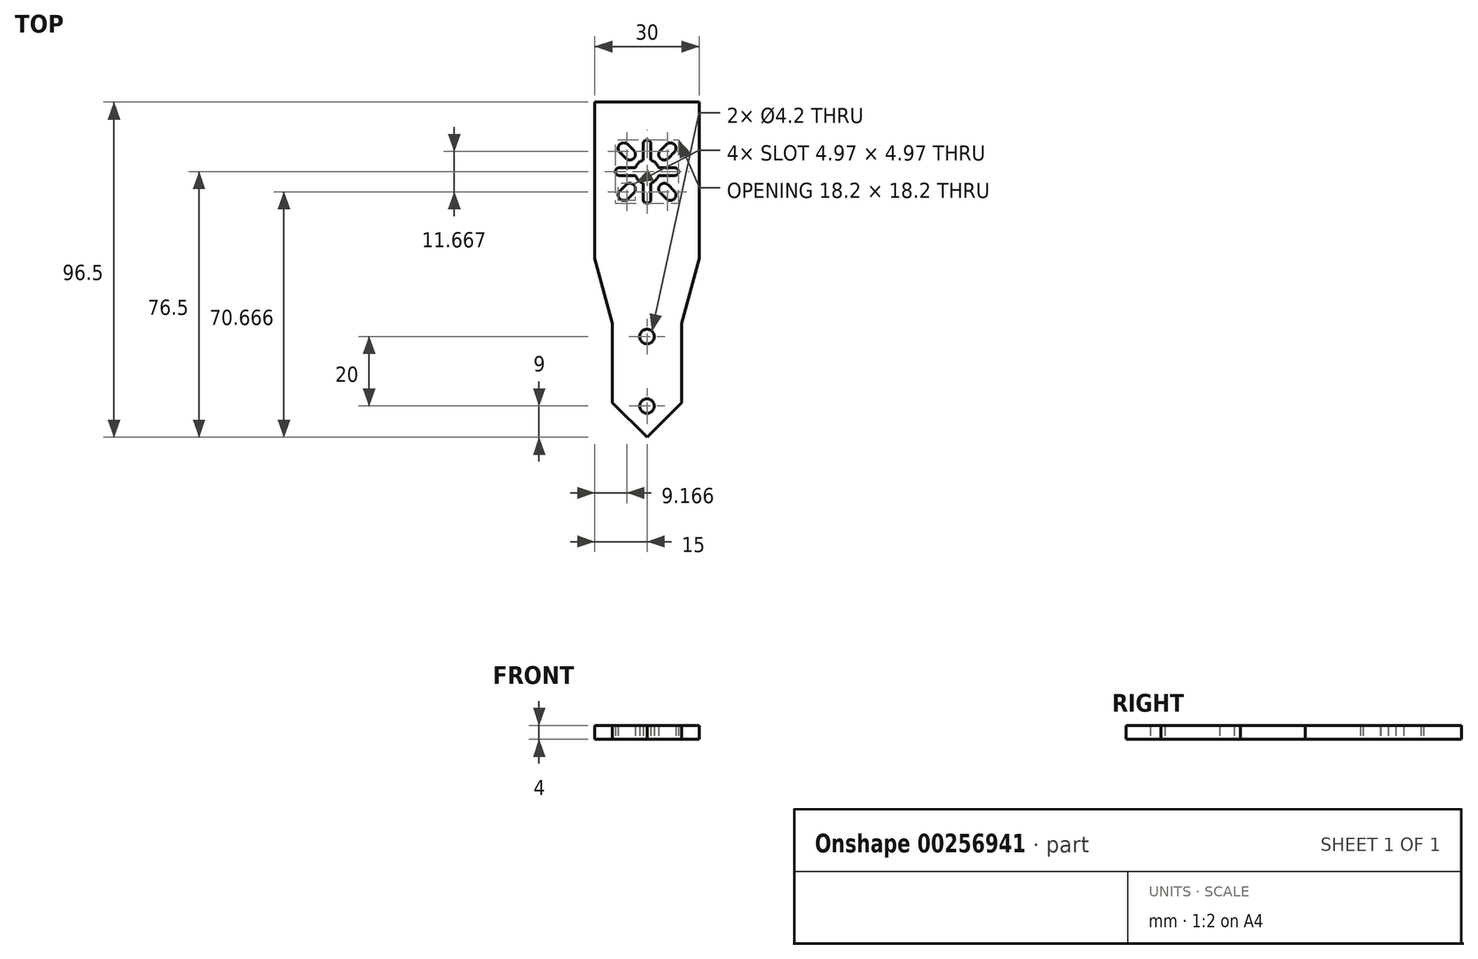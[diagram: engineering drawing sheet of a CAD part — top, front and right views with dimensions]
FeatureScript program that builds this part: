
annotation { "Feature Type Name" : "Feature", "Feature Type Description" : "" }
export const myFeature = defineFeature(function(context is Context, id is Id, definition is map)
    precondition{}
    {
        {
            var Q0;
            Q0=qCreatedBy(makeId("Top.planeOp"),FACE);
            var sketch = newSketch(context, id + "F0", { "sketchPlane" : qUnion([Q0])});
            skLineSegment(sketch, "E0", {"start": v(0, 77.5) * mm, "end": v(0, -77.5) * mm, "construction": true});
            skLineSegment(sketch, "E1", {"start": v(-10, 33.84) * mm, "end": v(-10, 11) * mm});
            skLineSegment(sketch, "E2", {"start": v(-10, 11) * mm, "end": v(0, 1) * mm});
            skLineSegment(sketch, "E3", {"start": v(-10, 33.84) * mm, "end": v(-15, 52.5) * mm});
            skLineSegment(sketch, "E4", {"start": v(-15, 52.5) * mm, "end": v(-15, 97.5) * mm});
            skLineSegment(sketch, "E5", {"start": v(-15, 97.5) * mm, "end": v(15, 97.5) * mm});
            skLineSegment(sketch, "E6.MirrorCS", {"start": v(15, 52.5) * mm, "end": v(15, 97.5) * mm});
            skLineSegment(sketch, "E7.MirrorCS", {"start": v(10, 33.84) * mm, "end": v(15, 52.5) * mm});
            skLineSegment(sketch, "E8.MirrorCS", {"start": v(10, 11) * mm, "end": v(0, 1) * mm});
            skLineSegment(sketch, "E9.MirrorCS", {"start": v(10, 33.84) * mm, "end": v(10, 11) * mm});
            skCircle(sketch, "E10", {"center": v(0, 10) * mm, "radius": 2.1 * mm});
            skCircle(sketch, "E11", {"center": v(0, 30) * mm, "radius": 2.1 * mm});
            skArc(sketch, "E12", {"start": v(-5.59, 85.35) * mm, "mid": v(-7.85, 85.35) * mm, "end": v(-7.85, 83.09) * mm});
            skArc(sketch, "E13", {"start": v(-6.08, 81.32) * mm, "mid": v(-3.82, 81.32) * mm, "end": v(-3.82, 83.58) * mm});
            skLineSegment(sketch, "E14", {"start": v(-5.59, 85.35) * mm, "end": v(-3.82, 83.58) * mm});
            skLineSegment(sketch, "E15", {"start": v(-7.85, 83.09) * mm, "end": v(-6.08, 81.32) * mm});
            skArc(sketch, "E16", {"start": v(-1.1, 80.82) * mm, "mid": v(-2.47, 79.97) * mm, "end": v(-3.32, 78.6) * mm});
            skArc(sketch, "E17", {"start": v(1.1, 85.5) * mm, "mid": v(0, 86.6) * mm, "end": v(-1.1, 85.5) * mm});
            skLineSegment(sketch, "E18", {"start": v(-1.1, 85.5) * mm, "end": v(-1.1, 80.82) * mm});
            skLineSegment(sketch, "E19", {"start": v(1.1, 85.5) * mm, "end": v(1.1, 80.82) * mm});
            skArc(sketch, "E20.1.0", {"start": v(-8, 78.6) * mm, "mid": v(-9.1, 77.5) * mm, "end": v(-8, 76.4) * mm});
            skArc(sketch, "E20.1.1", {"start": v(-7.85, 71.91) * mm, "mid": v(-7.85, 69.65) * mm, "end": v(-5.59, 69.65) * mm});
            skLineSegment(sketch, "E20.1.2", {"start": v(-7.85, 71.91) * mm, "end": v(-6.08, 73.68) * mm});
            skArc(sketch, "E20.1.3", {"start": v(-3.82, 71.42) * mm, "mid": v(-3.82, 73.68) * mm, "end": v(-6.08, 73.68) * mm});
            skLineSegment(sketch, "E20.1.4", {"start": v(-5.59, 69.65) * mm, "end": v(-3.82, 71.42) * mm});
            skLineSegment(sketch, "E20.1.5", {"start": v(-8, 78.6) * mm, "end": v(-3.32, 78.6) * mm});
            skLineSegment(sketch, "E20.1.6", {"start": v(-8, 76.4) * mm, "end": v(-3.32, 76.4) * mm});
            skArc(sketch, "E20.2.0", {"start": v(-1.1, 69.5) * mm, "mid": v(0, 68.4) * mm, "end": v(1.1, 69.5) * mm});
            skArc(sketch, "E20.2.1", {"start": v(5.59, 69.65) * mm, "mid": v(7.85, 69.65) * mm, "end": v(7.85, 71.91) * mm});
            skLineSegment(sketch, "E20.2.2", {"start": v(5.59, 69.65) * mm, "end": v(3.82, 71.42) * mm});
            skArc(sketch, "E20.2.3", {"start": v(6.08, 73.68) * mm, "mid": v(3.82, 73.68) * mm, "end": v(3.82, 71.42) * mm});
            skLineSegment(sketch, "E20.2.4", {"start": v(7.85, 71.91) * mm, "end": v(6.08, 73.68) * mm});
            skLineSegment(sketch, "E20.2.5", {"start": v(-1.1, 69.5) * mm, "end": v(-1.1, 74.18) * mm});
            skLineSegment(sketch, "E20.2.6", {"start": v(1.1, 69.5) * mm, "end": v(1.1, 74.18) * mm});
            skArc(sketch, "E21.4.3.0", {"start": v(7.85, 83.09) * mm, "mid": v(7.85, 85.35) * mm, "end": v(5.59, 85.35) * mm});
            skArc(sketch, "E21.7.3.0", {"start": v(8, 76.4) * mm, "mid": v(9.1, 77.5) * mm, "end": v(8, 78.6) * mm});
            skLineSegment(sketch, "E21.8.3.0", {"start": v(7.85, 83.09) * mm, "end": v(6.08, 81.32) * mm});
            skArc(sketch, "E21.11.3.0", {"start": v(3.82, 83.58) * mm, "mid": v(3.82, 81.32) * mm, "end": v(6.08, 81.32) * mm});
            skLineSegment(sketch, "E21.15.3.0", {"start": v(5.59, 85.35) * mm, "end": v(3.82, 83.58) * mm});
            skLineSegment(sketch, "E21.18.3.0", {"start": v(8, 76.4) * mm, "end": v(3.32, 76.4) * mm});
            skLineSegment(sketch, "E21.21.3.0", {"start": v(8, 78.6) * mm, "end": v(3.32, 78.6) * mm});
            skArc(sketch, "E22.trimOffspring", {"start": v(-3.32, 76.4) * mm, "mid": v(-2.47, 75.03) * mm, "end": v(-1.1, 74.18) * mm});
            skArc(sketch, "E23.trimOffspring", {"start": v(1.1, 74.18) * mm, "mid": v(2.47, 75.03) * mm, "end": v(3.32, 76.4) * mm});
            skArc(sketch, "E24.trimOffspring", {"start": v(3.32, 78.6) * mm, "mid": v(2.47, 79.97) * mm, "end": v(1.1, 80.82) * mm});
            skLineSegment(sketch, "E25", {"start": v(-6.72, 84.22) * mm, "end": v(-4.95, 82.45) * mm, "construction": true});
            skLineSegment(sketch, "E26", {"start": v(4.95, 72.55) * mm, "end": v(6.72, 70.78) * mm, "construction": true});
            skSolve(sketch);
        }
        {
            var Q0;
            Q0 = qSketchRegion(id + "F0", true);
            extrude(context, id + "F1", {"entities" : qUnion([Q0]), "depth" : 4 * mm});
        }
    });
